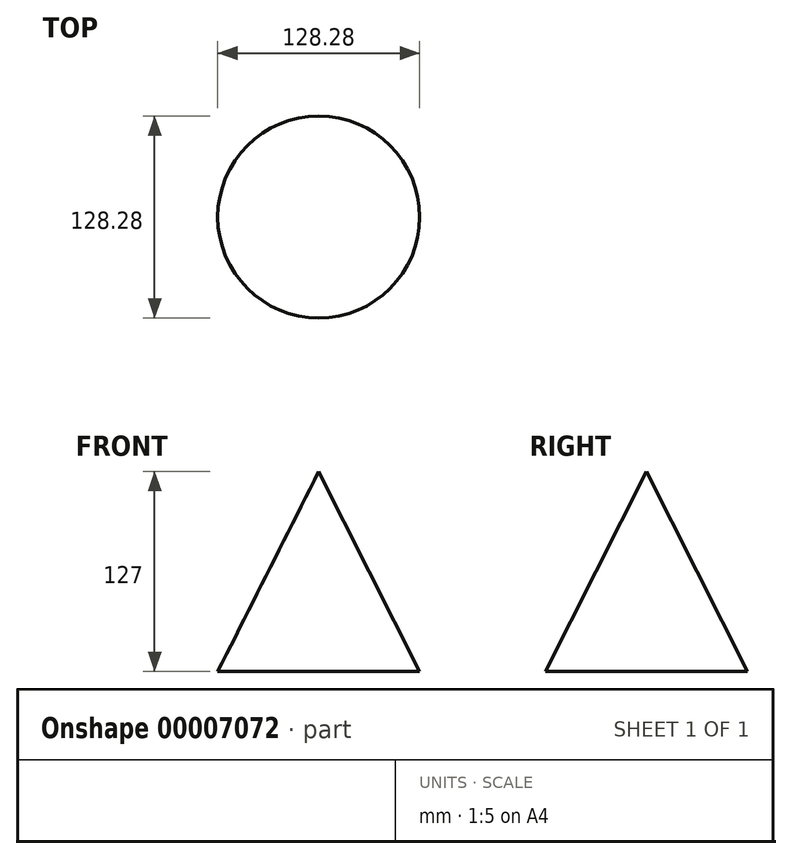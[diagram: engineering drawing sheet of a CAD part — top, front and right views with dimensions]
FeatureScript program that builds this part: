
annotation { "Feature Type Name" : "Feature", "Feature Type Description" : "" }
export const myFeature = defineFeature(function(context is Context, id is Id, definition is map)
    precondition{}
    {
        {
            var Q0;
            Q0=qCreatedBy(makeId("Top.planeOp"),FACE);
            var sketch = newSketch(context, id + "F0", { "sketchPlane" : qUnion([Q0])});
            skCircle(sketch, "E0", {"center": v(0, 0) * mm, "radius": 64.14 * mm});
            skSolve(sketch);
        }
        {
            var Q0;
            Q0=qCreatedBy(makeId("Top.planeOp"),FACE);
            cPlane(context, id + "F1", {"entities" : qUnion([Q0]), "cplaneType" : CPlaneType.OFFSET, "offset" : 127 * mm, "width" : 152.4 * mm, "height" : 152.4 * mm});
        }
        {
            var Q0;
            Q0=qCreatedBy(id+"F1.planeOp",FACE);
            var sketch = newSketch(context, id + "F2", { "sketchPlane" : qUnion([Q0])});
            skPoint(sketch, "E1.0", {"position": v(0, 0) * mm});
            skSolve(sketch);
        }
        {
            var Q0;
            Q0=makeQuery(id+"F0.imprint","IMPRINT",FACE,{"disambiguationData":[TD([[makeQuery(id+"F0.imprint","IMPRINT",EDGE,{"derivedFrom":sQuery(id+"F0.wireOp",EDGE,"E0")}),1.0]])]});
            var Q1;
            Q1=sQuery(id+"F2.wireOp",VERTEX,"E1.0");
            loft(context, id + "F3", {"sheetProfilesArray" : [{ "sheetProfileEntities" : qUnion([Q0]) }, { "sheetProfileEntities" : qUnion([Q1]) }]});
        }
    });
